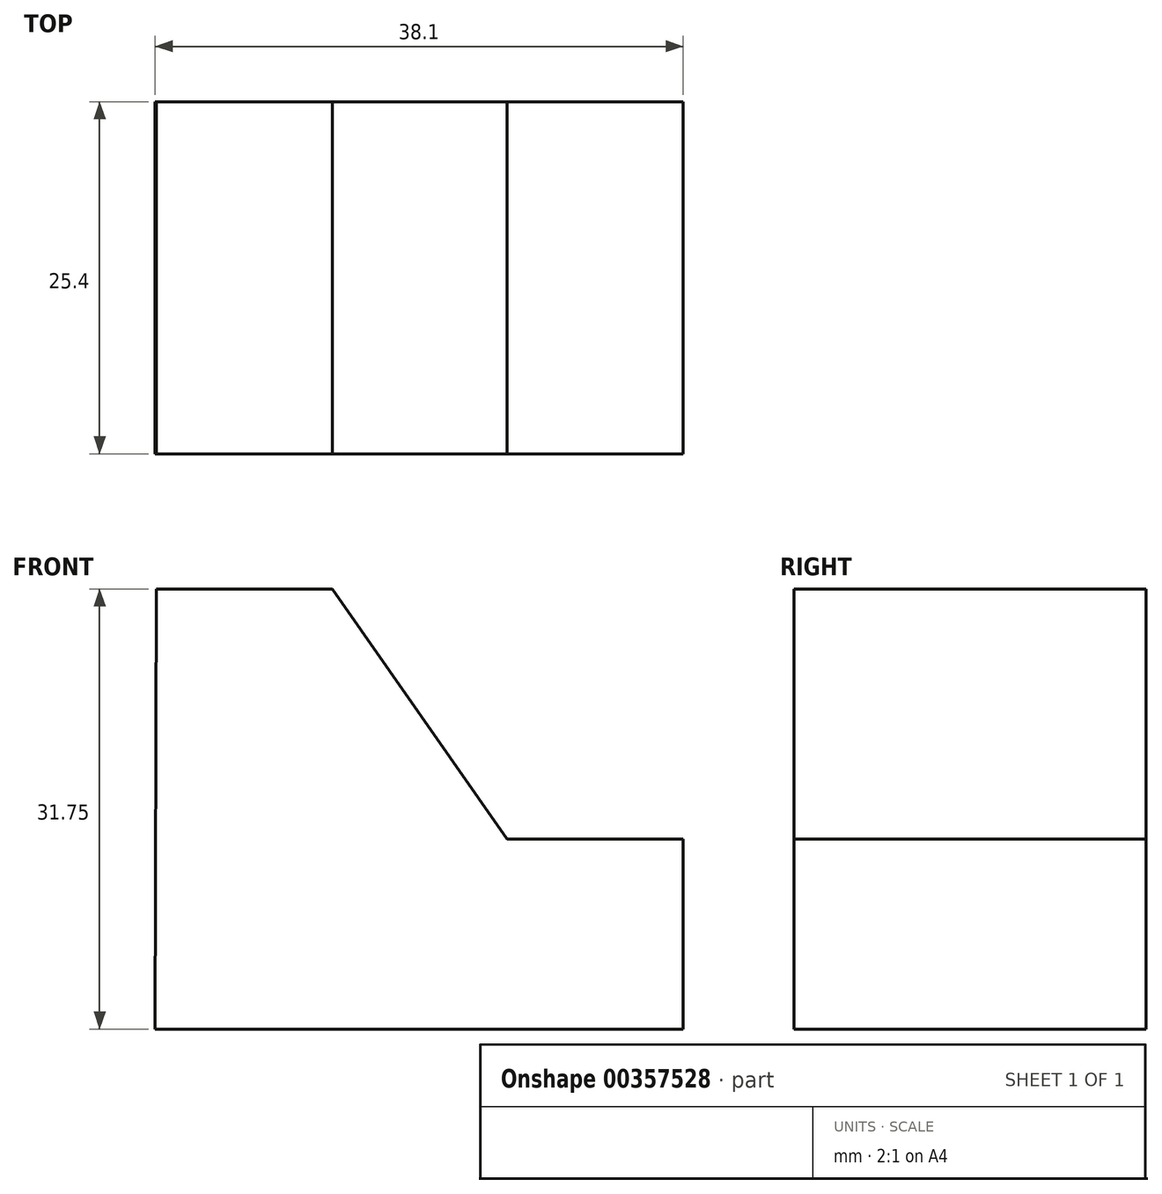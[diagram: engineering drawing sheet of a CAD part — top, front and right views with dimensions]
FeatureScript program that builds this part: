
annotation { "Feature Type Name" : "Feature", "Feature Type Description" : "" }
export const myFeature = defineFeature(function(context is Context, id is Id, definition is map)
    precondition{}
    {
        {
            var Q0;
            Q0=qCreatedBy(makeId("Front.planeOp"),FACE);
            var sketch = newSketch(context, id + "F0", { "sketchPlane" : qUnion([Q0])});
            skLineSegment(sketch, "E0", {"start": v(-46.18, -41.1) * mm, "end": v(-8.08, -41.1) * mm});
            skLineSegment(sketch, "E1", {"start": v(-8.08, -41.1) * mm, "end": v(-8.08, -27.38) * mm});
            skLineSegment(sketch, "E2", {"start": v(-8.08, -27.38) * mm, "end": v(-20.78, -27.38) * mm});
            skLineSegment(sketch, "E3", {"start": v(-20.78, -27.38) * mm, "end": v(-33.39, -9.35) * mm});
            skLineSegment(sketch, "E4", {"start": v(-33.39, -9.35) * mm, "end": v(-46.09, -9.35) * mm});
            skLineSegment(sketch, "E5", {"start": v(-46.18, -41.1) * mm, "end": v(-46.09, -9.35) * mm});
            skSolve(sketch);
        }
        {
            var Q0;
            Q0=makeQuery(id+"F0.imprint","IMPRINT",FACE,{"disambiguationData":[TD([[makeQuery(id+"F0.imprint","IMPRINT",EDGE,{"derivedFrom":sQuery(id+"F0.wireOp",EDGE,"E0")}),1.0]])]});
            extrude(context, id + "F1", {"entities" : qUnion([Q0]), "depth" : 25.4 * mm});
        }
    });
